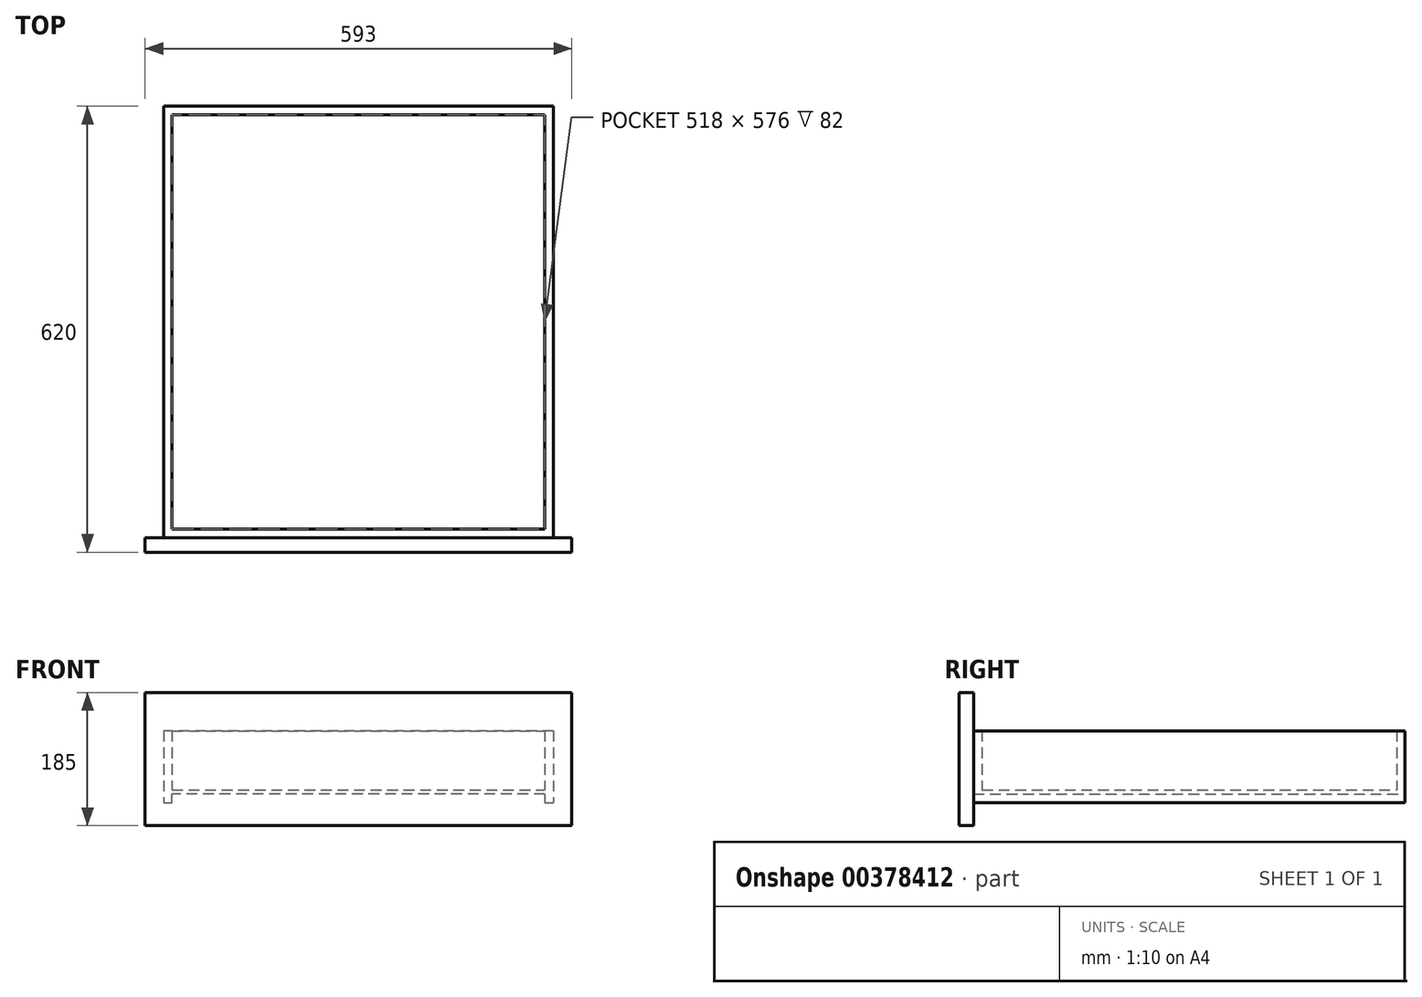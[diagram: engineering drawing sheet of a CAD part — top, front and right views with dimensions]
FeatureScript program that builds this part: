
annotation { "Feature Type Name" : "Feature", "Feature Type Description" : "" }
export const myFeature = defineFeature(function(context is Context, id is Id, definition is map)
    precondition{}
    {
        {
            var Q0;
            Q0=qCreatedBy(makeId("Front.planeOp"),FACE);
            var sketch = newSketch(context, id + "F0", { "sketchPlane" : qUnion([Q0])});
            skLineSegment(sketch, "E0.bottom", {"start": v(259, 3) * mm, "end": v(-259, 3) * mm});
            skLineSegment(sketch, "E0.top", {"start": v(259, -3) * mm, "end": v(-259, -3) * mm});
            skLineSegment(sketch, "E0.left", {"start": v(259, 3) * mm, "end": v(259, -3) * mm});
            skLineSegment(sketch, "E0.right", {"start": v(-259, 3) * mm, "end": v(-259, -3) * mm});
            skPoint(sketch, "E0.middle", {"position": v(0, 0) * mm});
            skLineSegment(sketch, "E1", {"start": v(-259, 3) * mm, "end": v(-259, 85) * mm});
            skLineSegment(sketch, "E2", {"start": v(-259, 85) * mm, "end": v(-271, 85) * mm});
            skLineSegment(sketch, "E3", {"start": v(-271, 85) * mm, "end": v(-271, -15) * mm});
            skLineSegment(sketch, "E4", {"start": v(-271, -15) * mm, "end": v(-259, -15) * mm});
            skLineSegment(sketch, "E5", {"start": v(-259, -15) * mm, "end": v(-259, -3) * mm});
            skLineSegment(sketch, "E6.bottom", {"start": v(259, 85) * mm, "end": v(271, 85) * mm});
            skLineSegment(sketch, "E6.top", {"start": v(259, -15) * mm, "end": v(271, -15) * mm});
            skLineSegment(sketch, "E6.left", {"start": v(259, 85) * mm, "end": v(259, -15) * mm});
            skLineSegment(sketch, "E6.right", {"start": v(271, 85) * mm, "end": v(271, -15) * mm});
            skSolve(sketch);
        }
        {
            var Q0;
            Q0=qSketchRegion(id+"F0",true);
            extrude(context, id + "F1", {"entities" : qUnion([Q0]), "depth" : 600 * mm});
        }
        {
            var Q0;
            {var subQ0=sQuery(id+"F0.wireOp",EDGE,"E6.left");Q0=makeQuery(id+"F1.opExtrude","SWEPT_FACE",FACE,{"disambiguationData":[OSD([subQ0]),TDD([makeQuery(id+"F0.imprint","IMPRINT",EDGE,{"disambiguationData":[TD([[makeQuery(id+"F0.imprint","INTERSECT",VERTEX,{"derivedFrom":[sQuery(id+"F0.wireOp",EDGE,"E0.bottom"),subQ0]}),1.0]])],"derivedFrom":subQ0})])]});}
            var sketch = newSketch(context, id + "F2", { "sketchPlane" : qUnion([Q0])});
            skLineSegment(sketch, "E7.bottom", {"start": v(0, 85) * mm, "end": v(12, 85) * mm});
            skLineSegment(sketch, "E7.top", {"start": v(0, 3) * mm, "end": v(12, 3) * mm});
            skLineSegment(sketch, "E7.left", {"start": v(0, 85) * mm, "end": v(0, 3) * mm});
            skLineSegment(sketch, "E7.right", {"start": v(12, 85) * mm, "end": v(12, 3) * mm});
            skLineSegment(sketch, "E8.bottom", {"start": v(600, 85) * mm, "end": v(588, 85) * mm});
            skLineSegment(sketch, "E8.top", {"start": v(600, 3) * mm, "end": v(588, 3) * mm});
            skLineSegment(sketch, "E8.left", {"start": v(600, 85) * mm, "end": v(600, 3) * mm});
            skLineSegment(sketch, "E8.right", {"start": v(588, 85) * mm, "end": v(588, 3) * mm});
            skSolve(sketch);
        }
        {
            var Q0;
            Q0=qSketchRegion(id+"F2",true);
            extrude(context, id + "F3", {"entities" : qUnion([Q0]), "operationType" : NewBodyOperationType.ADD, "depth" : 518 * mm});
        }
        {
            var Q0;
            Q0=makeQuery(id+"F3.boolean.opBoolean","MERGE",FACE,{"derivedFrom":[makeQuery(id+"F1.opExtrude","CAP_FACE",FACE,{"disambiguationData":[OSD([sQuery(id+"F0.wireOp",EDGE,"E0.bottom"),sQuery(id+"F0.wireOp",EDGE,"E0.top"),sQuery(id+"F0.wireOp",EDGE,"E1"),sQuery(id+"F0.wireOp",EDGE,"E2"),sQuery(id+"F0.wireOp",EDGE,"E3"),sQuery(id+"F0.wireOp",EDGE,"E4"),sQuery(id+"F0.wireOp",EDGE,"E5"),sQuery(id+"F0.wireOp",EDGE,"E6.bottom"),sQuery(id+"F0.wireOp",EDGE,"E6.top"),sQuery(id+"F0.wireOp",EDGE,"E6.left"),sQuery(id+"F0.wireOp",EDGE,"E6.right")])],"isStart":false}),makeQuery(id+"F3.opExtrude","SWEPT_FACE",FACE,{"disambiguationData":[OSD([sQuery(id+"F2.wireOp",EDGE,"E8.left")])]})]});
            var sketch = newSketch(context, id + "F4", { "sketchPlane" : qUnion([Q0])});
            skLineSegment(sketch, "E9.bottom", {"start": v(-296.5, 138.5) * mm, "end": v(296.5, 138.5) * mm});
            skLineSegment(sketch, "E9.top", {"start": v(-296.5, -46.5) * mm, "end": v(296.5, -46.5) * mm});
            skLineSegment(sketch, "E9.left", {"start": v(-296.5, 138.5) * mm, "end": v(-296.5, -46.5) * mm});
            skLineSegment(sketch, "E9.right", {"start": v(296.5, 138.5) * mm, "end": v(296.5, -46.5) * mm});
            skSolve(sketch);
        }
        {
            var Q0;
            Q0=qSketchRegion(id+"F4",true);
            extrude(context, id + "F5", {"entities" : qUnion([Q0]), "operationType" : NewBodyOperationType.ADD, "depth" : 20 * mm});
        }
    });
